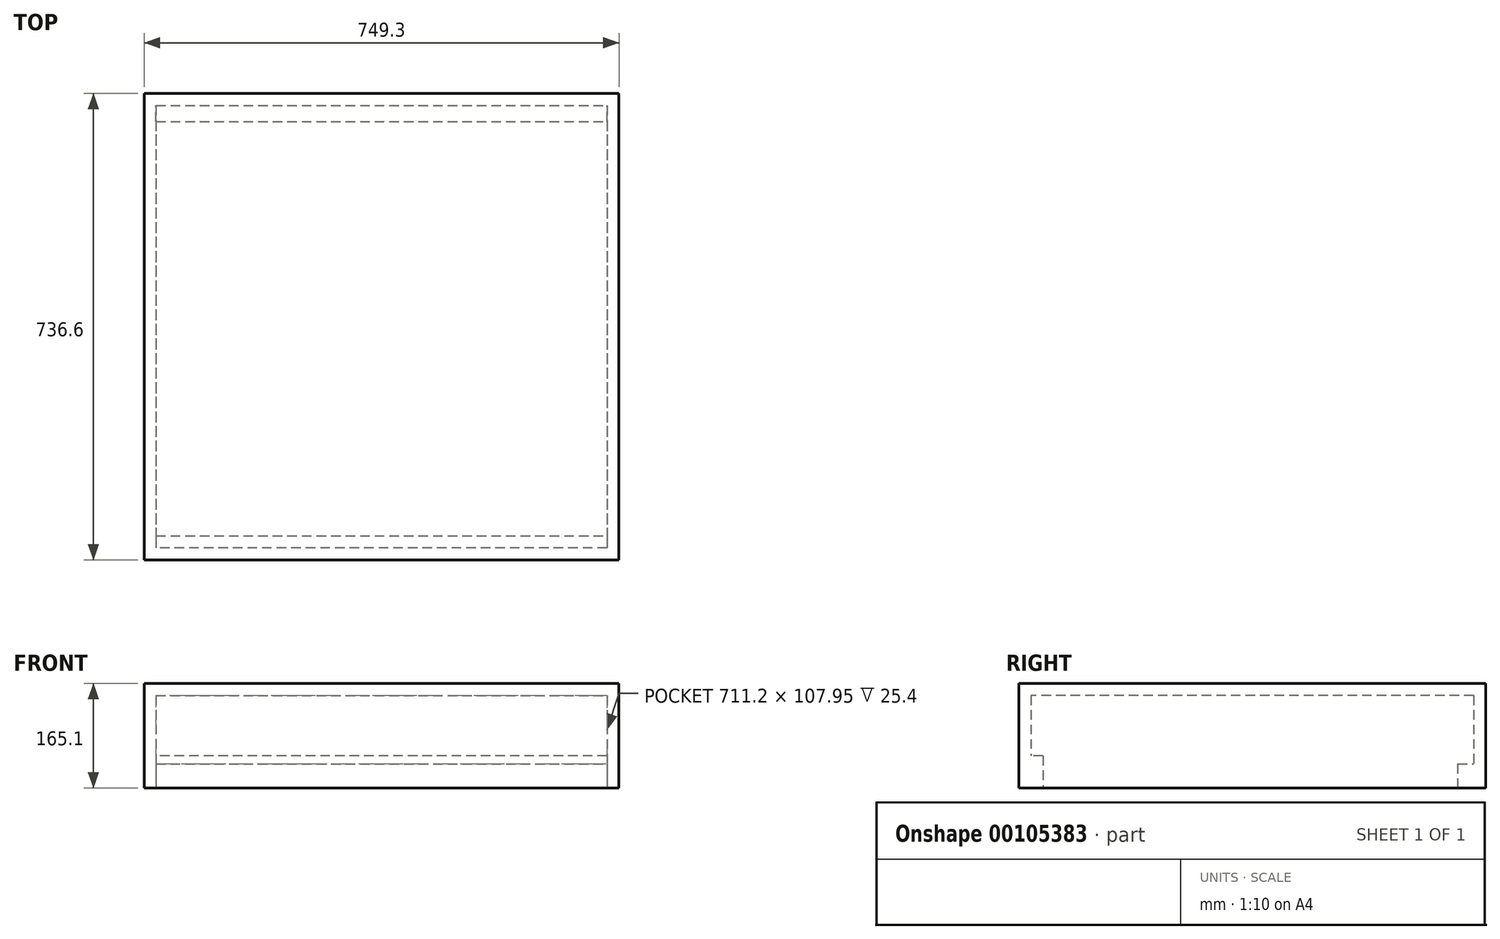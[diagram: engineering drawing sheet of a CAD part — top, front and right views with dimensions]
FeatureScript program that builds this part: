
annotation { "Feature Type Name" : "Feature", "Feature Type Description" : "" }
export const myFeature = defineFeature(function(context is Context, id is Id, definition is map)
    precondition{}
    {
        {
            var Q0;
            Q0=qCreatedBy(makeId("Top.planeOp"),FACE);
            var sketch = newSketch(context, id + "F0", { "sketchPlane" : qUnion([Q0])});
            skLineSegment(sketch, "E0.bottom", {"start": v(-391.82, 540.17) * mm, "end": v(357.48, 540.17) * mm});
            skLineSegment(sketch, "E0.top", {"start": v(-391.82, -196.43) * mm, "end": v(357.48, -196.43) * mm});
            skLineSegment(sketch, "E0.left", {"start": v(-391.82, 540.17) * mm, "end": v(-391.82, -196.43) * mm});
            skLineSegment(sketch, "E0.right", {"start": v(357.48, 540.17) * mm, "end": v(357.48, -196.43) * mm});
            skSolve(sketch);
        }
        {
            var Q0;
            Q0=makeQuery(id+"F0.imprint","IMPRINT",FACE,{"disambiguationData":[TD([[makeQuery(id+"F0.imprint","IMPRINT",EDGE,{"derivedFrom":sQuery(id+"F0.wireOp",EDGE,"E0.bottom")}),-1.0]])]});
            extrude(context, id + "F1", {"entities" : qUnion([Q0]), "depth" : 165.1 * mm});
        }
        {
            var Q0;
            Q0=makeQuery(id+"F1.opExtrude","CAP_FACE",FACE,{"disambiguationData":[OSD([sQuery(id+"F0.wireOp",EDGE,"E0.bottom"),sQuery(id+"F0.wireOp",EDGE,"E0.top"),sQuery(id+"F0.wireOp",EDGE,"E0.left"),sQuery(id+"F0.wireOp",EDGE,"E0.right")])],"isStart":true});
            shell(context, id + "F2", {"entities" : qUnion([Q0]), "thickness" : 19.05 * mm});
        }
        {
            var Q0;
            Q0=makeQuery(id+"F2.opShell","OFFSET_FACE",FACE,{"disambiguationData":[OSD([sQuery(id+"F0.wireOp",EDGE,"E0.bottom")])]});
            var sketch = newSketch(context, id + "F3", { "sketchPlane" : qUnion([Q0])});
            skLineSegment(sketch, "E1.bottom", {"start": v(-372.77, 0) * mm, "end": v(338.43, 0) * mm});
            skLineSegment(sketch, "E1.top", {"start": v(-372.77, 38.1) * mm, "end": v(338.43, 38.1) * mm});
            skLineSegment(sketch, "E1.left", {"start": v(-372.77, 0) * mm, "end": v(-372.77, 38.1) * mm});
            skLineSegment(sketch, "E1.right", {"start": v(338.43, 0) * mm, "end": v(338.43, 38.1) * mm});
            skSolve(sketch);
        }
        {
            var Q0;
            Q0 = qSketchRegion(id + "F3", true);
            extrude(context, id + "F4", {"entities" : qUnion([Q0]), "operationType" : NewBodyOperationType.ADD, "depth" : 25.4 * mm});
        }
        {
            var Q0;
            Q0=makeQuery(id+"F2.opShell","OFFSET_FACE",FACE,{"disambiguationData":[OSD([sQuery(id+"F0.wireOp",EDGE,"E0.top")])]});
            var sketch = newSketch(context, id + "F5", { "sketchPlane" : qUnion([Q0])});
            skLineSegment(sketch, "E2.bottom", {"start": v(-338.43, 0) * mm, "end": v(372.77, 0) * mm});
            skLineSegment(sketch, "E2.top", {"start": v(-338.43, 50.8) * mm, "end": v(372.77, 50.8) * mm});
            skLineSegment(sketch, "E2.left", {"start": v(-338.43, 0) * mm, "end": v(-338.43, 50.8) * mm});
            skLineSegment(sketch, "E2.right", {"start": v(372.77, 0) * mm, "end": v(372.77, 50.8) * mm});
            skSolve(sketch);
        }
        {
            var Q0;
            Q0 = qSketchRegion(id + "F5", true);
            extrude(context, id + "F6", {"entities" : qUnion([Q0]), "operationType" : NewBodyOperationType.ADD, "depth" : 19.05 * mm});
        }
    });
